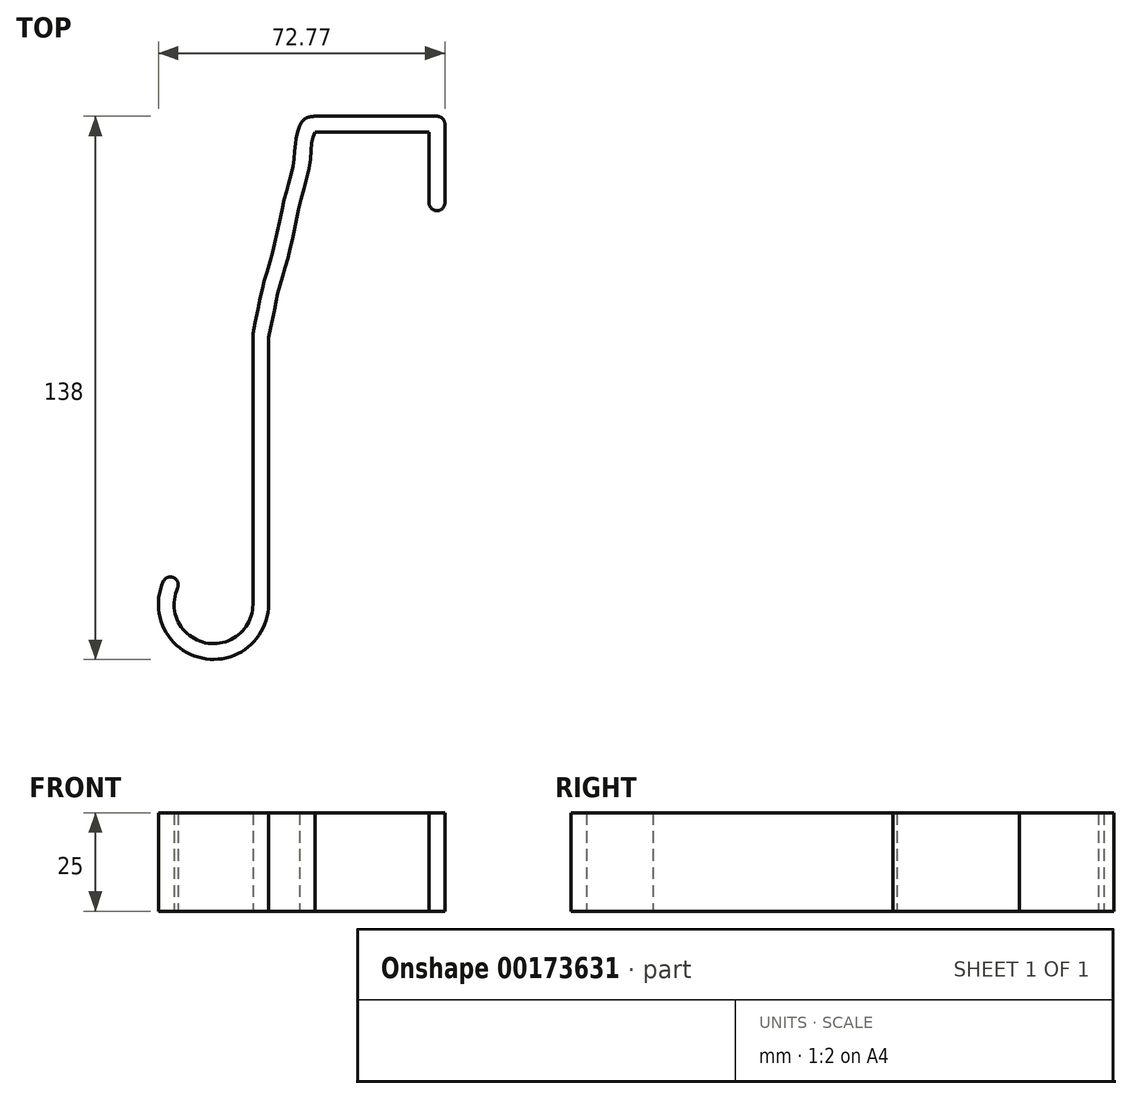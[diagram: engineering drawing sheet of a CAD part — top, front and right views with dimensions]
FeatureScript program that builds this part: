
annotation { "Feature Type Name" : "Feature", "Feature Type Description" : "" }
export const myFeature = defineFeature(function(context is Context, id is Id, definition is map)
    precondition{}
    {
        {
            var Q0;
            Q0=qCreatedBy(makeId("Top.planeOp"),FACE);
            var sketch = newSketch(context, id + "F0", { "sketchPlane" : qUnion([Q0])});
            skLineSegment(sketch, "E0.bottom", {"start": v(9.44, 0) * mm, "end": v(13.44, 0) * mm});
            skLineSegment(sketch, "E0.top", {"start": v(11.44, -20) * mm, "end": v(11.44, -20) * mm});
            skLineSegment(sketch, "E0.left", {"start": v(9.44, 0) * mm, "end": v(9.44, -18) * mm});
            skLineSegment(sketch, "E0.right", {"start": v(13.44, 0) * mm, "end": v(13.44, -18) * mm});
            skLineSegment(sketch, "E1.bottom", {"start": v(13.44, 0) * mm, "end": v(-19.56, 0) * mm});
            skLineSegment(sketch, "E1.top", {"start": v(11.44, 4) * mm, "end": v(-19.56, 4) * mm});
            skLineSegment(sketch, "E1.left", {"start": v(13.44, 0) * mm, "end": v(13.44, 2) * mm});
            skLineSegment(sketch, "E1.right", {"start": v(-19.56, 0) * mm, "end": v(-19.56, 4) * mm});
            skFitSpline(sketch, "E2", {"points": [v(-19.56, 0) * mm, v(-20.32, -2.52) * mm, v(-20.83, -8.08) * mm, v(-22.91, -16.45) * mm, v(-24.84, -25.05) * mm, v(-26.62, -32.68) * mm, v(-28.62, -39.58) * mm, v(-29.88, -45.28) * mm, v(-31.33, -52.18) * mm], "startDerivative": vector(-11.19, -28.69) * mm, "endDerivative": vector(-12.7, -54.6) * mm});
            skFitSpline(sketch, "E3.0", {"points": [v(-23.4, 1.5) * mm, v(-23.52, 1.2) * mm, v(-23.73, 0.67) * mm, v(-24.02, -0.2) * mm, v(-24.18, -0.83) * mm, v(-24.3, -1.36) * mm, v(-24.38, -1.78) * mm, v(-24.45, -2.2) * mm, v(-24.5, -2.62) * mm, v(-24.54, -3.02) * mm, v(-24.59, -3.55) * mm, v(-24.65, -4.46) * mm, v(-24.7, -5.46) * mm, v(-24.8, -6.43) * mm, v(-24.87, -7.15) * mm, v(-24.97, -7.84) * mm, v(-25.11, -8.58) * mm, v(-25.28, -9.36) * mm, v(-25.55, -10.46) * mm, v(-25.86, -11.62) * mm, v(-26.2, -12.84) * mm, v(-26.46, -13.78) * mm, v(-26.73, -14.74) * mm, v(-26.99, -15.73) * mm, v(-27.24, -16.7) * mm, v(-27.55, -18.01) * mm, v(-27.91, -19.62) * mm, v(-28.32, -21.5) * mm, v(-28.7, -23.35) * mm, v(-29.07, -25.13) * mm, v(-29.44, -26.86) * mm, v(-29.82, -28.55) * mm, v(-30.16, -29.92) * mm, v(-30.44, -31) * mm, v(-30.73, -32.07) * mm, v(-31.12, -33.43) * mm, v(-31.62, -35.09) * mm, v(-32.03, -36.47) * mm, v(-32.35, -37.58) * mm, v(-32.58, -38.42) * mm, v(-32.8, -39.25) * mm, v(-33.06, -40.33) * mm, v(-33.35, -41.64) * mm, v(-33.67, -43.17) * mm, v(-34.07, -45.22) * mm, v(-34.62, -47.92) * mm, v(-35.1, -50.14) * mm, v(-35.35, -51.24) * mm]});
            skFitSpline(sketch, "E4", {"points": [v(-23.4, 1.5) * mm, v(-19.56, 4) * mm], "startDerivative": vector(2.9, 6.76) * mm, "endDerivative": vector(5.83, 0.66) * mm});
            skLineSegment(sketch, "E5", {"start": v(-31.33, -52.18) * mm, "end": v(-31.33, -120) * mm});
            skLineSegment(sketch, "E6.0", {"start": v(-35.33, -51.15) * mm, "end": v(-35.33, -120) * mm});
            skArc(sketch, "E7", {"start": v(-54.45, -115.88) * mm, "mid": v(-47.44, -129.78) * mm, "end": v(-35.33, -120) * mm});
            skArc(sketch, "E8", {"start": v(-58.1, -114.24) * mm, "mid": v(-48.28, -133.69) * mm, "end": v(-31.33, -120) * mm});
            skLineSegment(sketch, "E9", {"start": v(-55.15, -113.4) * mm, "end": v(-55.15, -113.4) * mm});
            skPoint(sketch, "E10.visualSharp", {"position": v(13.44, 4) * mm});
            skArc(sketch, "E10.filletArc", {"start": v(13.44, 2) * mm, "mid": v(12.86, 3.41) * mm, "end": v(11.44, 4) * mm});
            skPoint(sketch, "E11.visualSharp", {"position": v(9.44, -20) * mm});
            skArc(sketch, "E11.filletArc", {"start": v(9.44, -18) * mm, "mid": v(10.03, -19.41) * mm, "end": v(11.44, -20) * mm});
            skPoint(sketch, "E12.visualSharp", {"position": v(13.44, -20) * mm});
            skArc(sketch, "E12.filletArc", {"start": v(11.44, -20) * mm, "mid": v(12.86, -19.41) * mm, "end": v(13.44, -18) * mm});
            skPoint(sketch, "E13.visualSharp", {"position": v(-53.63, -114.42) * mm});
            skArc(sketch, "E13.filletArc", {"start": v(-54.45, -115.88) * mm, "mid": v(-54.35, -114.51) * mm, "end": v(-55.15, -113.4) * mm});
            skPoint(sketch, "E14.visualSharp", {"position": v(-56.95, -112.2) * mm});
            skArc(sketch, "E14.filletArc", {"start": v(-55.15, -113.4) * mm, "mid": v(-56.82, -113.14) * mm, "end": v(-58.1, -114.24) * mm});
            skSolve(sketch);
        }
        {
            var Q0;
            Q0=makeQuery(id+"F0.imprint","IMPRINT",FACE,{"disambiguationData":[TD([[makeQuery(id+"F0.imprint","IMPRINT",EDGE,{"derivedFrom":sQuery(id+"F0.wireOp",EDGE,"E1.right")}),1.0]])]});
            var Q1;
            Q1=makeQuery(id+"F0.imprint","IMPRINT",FACE,{"disambiguationData":[TD([[makeQuery(id+"F0.imprint","IMPRINT",EDGE,{"derivedFrom":sQuery(id+"F0.wireOp",EDGE,"E1.top")}),1.0]])]});
            var Q2;
            {var subQ1=sQuery(id+"F0.wireOp",EDGE,"E0.left");Q2=makeQuery(id+"F0.imprint","IMPRINT",FACE,{"disambiguationData":[TD([[makeQuery(id+"F0.imprint","IMPRINT",EDGE,{"derivedFrom":subQ1}),1.0]])]});}
            extrude(context, id + "F1", {"entities" : qUnion([Q0, Q1, Q2]), "depth" : 25 * mm});
        }
    });
